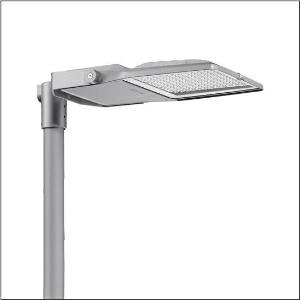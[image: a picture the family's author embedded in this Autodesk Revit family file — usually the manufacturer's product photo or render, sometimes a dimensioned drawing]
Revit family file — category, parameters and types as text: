
# Revit family: floodlight_fl_21_midi___pl64_5xa7786f2e3a_6eef
name_source: partatom
category: Lighting Fixtures
units: mm (PartAtom-declared; Revit-internal decimal feet)

## family parameters
Cut with Voids When Loaded = No
Host = Face
Light Source = No
Part Type = Normal
Room Calculation Point = No
Round Connector Dimension = Use Diameter
Shared = No

## types (1)
- --- (1 x LED, 34530 lm, 271.6 W, 3000K)
    Apparent Load = 272 VA
    CIE Flux Codes = 28 80 98 100 100
    Color Rendering = 70
    Color Temperature = 3000K
    Default Elevation = 1800 mm
    Description = Floodlight FL 21 midi, floodlight, primary light control with lens, of PMMA, primary optical cover: protective disc, of toughened safety glass, transparent, light distribution: PL64, light emission: direct distribution, installation type: surface-mounted, LED, High Power LED, rated luminous flux: 34.530lm, luminous efficacy: 127lm/W, light colour: 730, colour temperature: 3000K, control gear: ECG Smart Interface, control: flexible luminous flux parameterisation, time-dependent luminous flux control, constant luminous flux control, overheat protection, presetting dimming logarithmic, with terminal, 6-pole, mains connection: 220..240V, AC, 50/60Hz, start of lifetime: 272W, end of service life: 287W, reduction: 123W, luminaire housing, of diecast aluminium, powder-coated, Siteco® metallic grey (DB 702S), corrosivity category C5 mid according to DIN EN ISO 12944, sealing non-destructively replaceable, please order mast flange separately, mast bracket, of steel, galvanised, powder-coated, Siteco® metallic grey (DB 702S), Smart Interface below and above, protection rating (complete): IP66, insulation class (complete): insulation class II (safety insulation), certification: CE, protection symbol: D, impact resistance: IK08, permissible operating ambient temperature: -40..+40°C, permissible operating ambient temperature for outdoor applications: -40..+50°C, standard: DIN EN 12944, LABS conformity tested according to VDMA 24364:2018-05, packaging unit: 1 piece

Light Distribution: PL64
    Height = 76 mm
    Lamp = 1 x LED
    Lamp Light Flux = 34530 lm
    Lamp Power = 271.6 W
    Lamp count = 1
    Length = 657 mm
    Luminous efficacy = 127 lm/W
    Manufacturer = Siteco
    ModVariant = No
    Model = 5XA7786F2E3A
    Number of Poles = 1
    OnlyDefault = Yes
    Power Factor = 1
    Product Name = Floodlight FL 21 midi | PL64
    Product group = floodlight | pylon annexe
    ProductGroupID = 6200
    Protection Class = Protection class II
    Protection Degree = IP 66
    RLX_Detail_Level = 1
    RLX_Emergency_Light_Flux = 0 lm
    RLX_Emergency_Type = 0
    RLX_Emergency_Type_DB = No
    RlxData = <blob elided: 153565 chars, md5=2aab2890>
    Socket = socket
    Standby Power = 0 W
    System Light Flux = 34530 lm
    System Power = 272 W
    Type Comments = factory setting: luminous flux: 100 % | dim-lin: 254 | 620 mA
    Type Image = l_1007123.jpg
    URL = http://relux.com
    VarID = @adj_131603
    Voltage = 0 V
    Weight = 0.00 kg
    Width = 442 mm

## geometry (parser evidence)
native form markers: Blend x4, Sweep x15
no freeform markers — native parametric forms only
